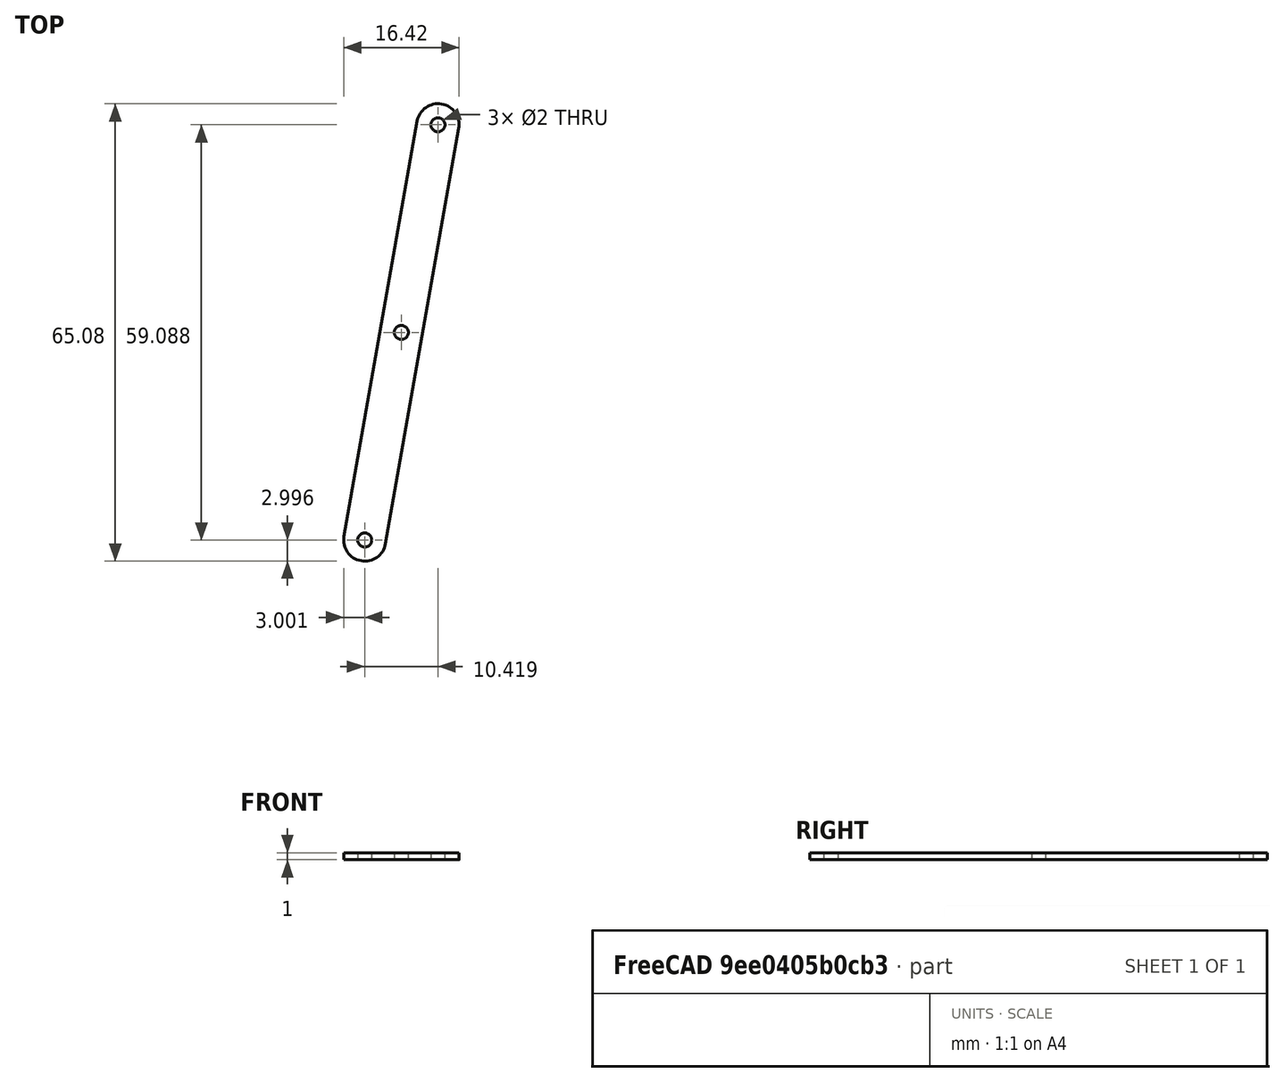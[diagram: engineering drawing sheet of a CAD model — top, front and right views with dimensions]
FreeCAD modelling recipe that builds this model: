
FCSTD DOCUMENT  (FreeCAD 0.19R24276 (Git))
Label: Center
License: All rights reserved
LicenseURL: http://en.wikipedia.org/wiki/All_rights_reserved
objects: Sketcher::SketchObject×1, PartDesign::Pad×1, PartDesign::Body×1
note: 4 computed .brp shape members not serialized (recipe doc carries the construction recipe); baked Part::Feature solids carry a one-line shape summary decoded from their .brp

FEATURE [Sketcher::SketchObject] Sketch
  FullyConstrained = true
  sketch-geometry (9):
    g0: ArcOfCircle CenterX=5.20945 CenterY=29.5442 CenterZ=0 NormalX=0 NormalY=0 NormalZ=1 AngleXU=0 Radius=3 StartAngle=6.10865 EndAngle=9.25025
    g1: ArcOfCircle CenterX=-5.20945 CenterY=-29.5442 CenterZ=0 NormalX=0 NormalY=0 NormalZ=1 AngleXU=0 Radius=3 StartAngle=2.96706 EndAngle=6.10865
    g2: LineSegment StartX=2.25502 StartY=30.0652 StartZ=0 EndX=-8.16387 EndY=-29.0233 EndZ=0
    g3: LineSegment StartX=8.16387 StartY=29.0233 StartZ=0 EndX=-2.25502 EndY=-30.0652 EndZ=0
    g4: LineSegment StartX=5.20945 StartY=29.5442 StartZ=0 EndX=-5.20945 EndY=-29.5442 EndZ=0
    g5: Circle CenterX=5.20945 CenterY=29.5442 CenterZ=0 NormalX=0 NormalY=0 NormalZ=1 AngleXU=0 Radius=1
    g6: Circle CenterX=-5.20945 CenterY=-29.5442 CenterZ=0 NormalX=0 NormalY=0 NormalZ=1 AngleXU=0 Radius=5e-16
    g7: Circle CenterX=0 CenterY=0 CenterZ=0 NormalX=0 NormalY=0 NormalZ=1 AngleXU=0 Radius=1
    g8: Circle CenterX=-5.20945 CenterY=-29.5442 CenterZ=0 NormalX=0 NormalY=0 NormalZ=1 AngleXU=0 Radius=1
  constraints (19):
    c: Tangent(g0,g3) = 1.5708
    c: Tangent(g0,g2) = -1.5708
    c: Tangent(g2,g1) = -1.5708
    c: Tangent(g3,g1) = 1.5708
    c: Equal(g0,g1)
    c: Coincident(g4,g0)
    c: Coincident(g4,g1)
    c: Coincident(g5,g0)
    c: Coincident(g6,g1)
    c: Tangent(g6,g4)
    c: Coincident(g8,g1)
    c: Symmetric(g0,g1,g7)
    c: Radius(g5) = 1
    c: Equal(g5,g7)
    c: Equal(g5,g8)
    c: Distance(g4) = 60
    c: Radius(g1) = 3
    c: Coincident(g7,g-1)
    c: Angle(g-2,g4) = -0.174533
FEATURE [PartDesign::Pad] Pad
  Direction = (1,1,1)
  Length = 1
  Length2 = 100
  Profile = -> Sketch
  Type = 0
FEATURE [PartDesign::Body] Body  label="Center_rotation_planka"
  Group = -> [Sketch,Pad]
  Origin = -> Origin
  Tip = -> Pad
